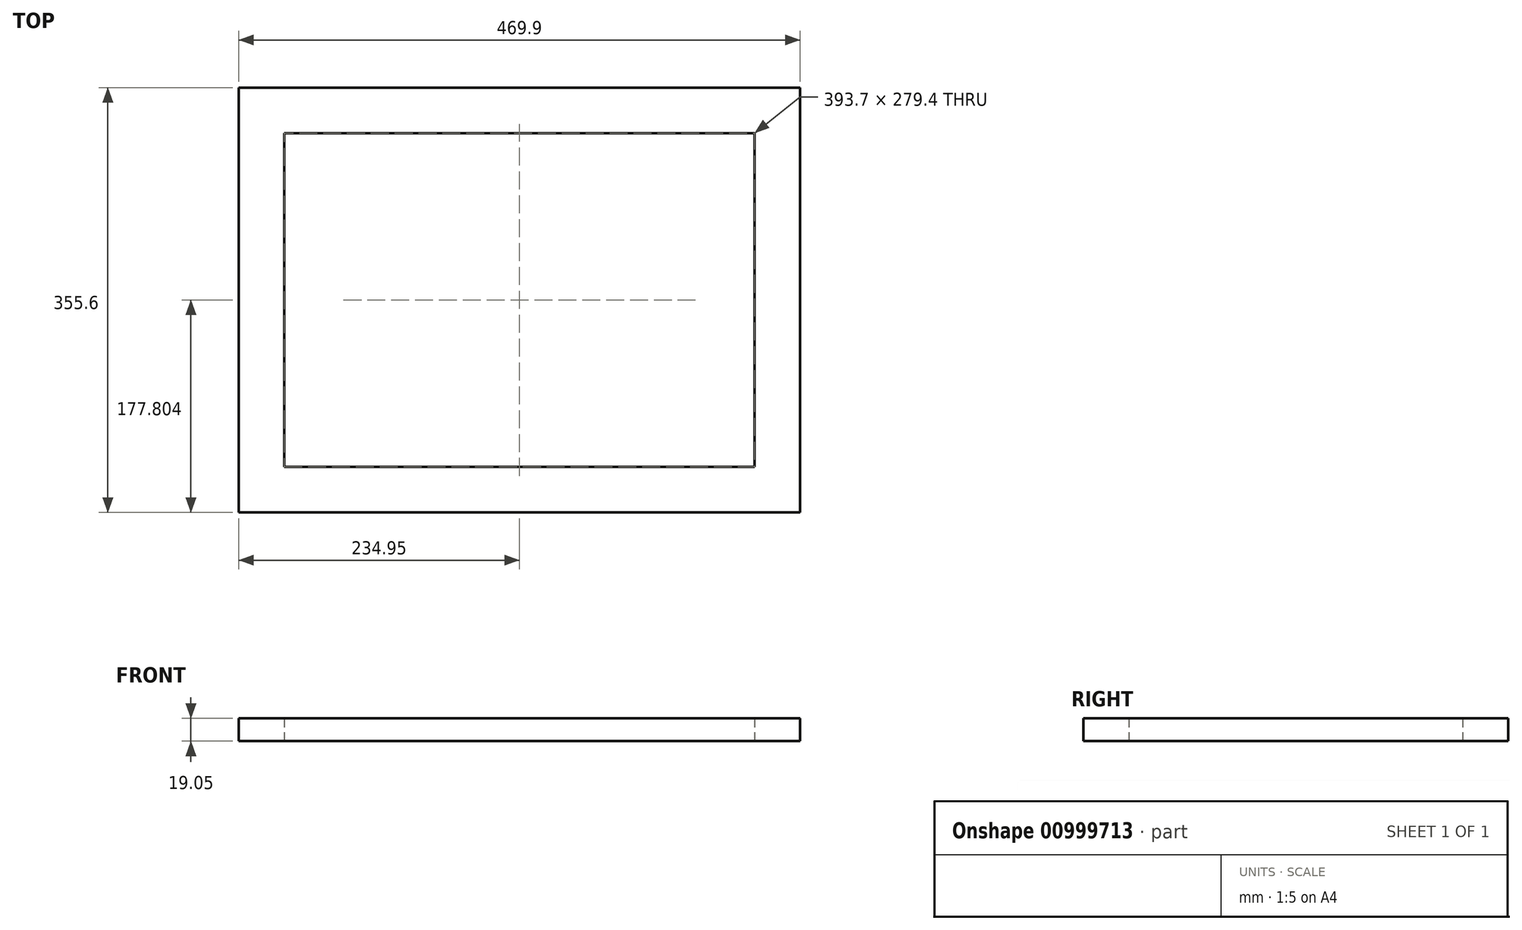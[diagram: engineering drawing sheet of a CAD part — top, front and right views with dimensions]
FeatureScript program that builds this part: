
annotation { "Feature Type Name" : "Feature", "Feature Type Description" : "" }
export const myFeature = defineFeature(function(context is Context, id is Id, definition is map)
    precondition{}
    {
        {
            var Q0;
            Q0=qCreatedBy(makeId("Top.planeOp"),FACE);
            var sketch = newSketch(context, id + "F0", { "sketchPlane" : qUnion([Q0])});
            skLineSegment(sketch, "E0.bottom", {"start": v(0, 20.24) * mm, "end": v(393.7, 20.24) * mm});
            skLineSegment(sketch, "E0.top", {"start": v(0, -17.86) * mm, "end": v(393.7, -17.86) * mm});
            skLineSegment(sketch, "E0.left", {"start": v(0, 20.24) * mm, "end": v(0, -17.86) * mm});
            skLineSegment(sketch, "E0.right", {"start": v(393.7, 20.24) * mm, "end": v(393.7, -17.86) * mm});
            skLineSegment(sketch, "E1.bottom", {"start": v(-38.1, 20.24) * mm, "end": v(0, 20.24) * mm});
            skLineSegment(sketch, "E1.top", {"start": v(-38.1, -335.36) * mm, "end": v(0, -335.36) * mm});
            skLineSegment(sketch, "E1.left", {"start": v(-38.1, 20.24) * mm, "end": v(-38.1, -335.36) * mm});
            skLineSegment(sketch, "E1.right", {"start": v(0, 20.24) * mm, "end": v(0, -335.36) * mm});
            skLineSegment(sketch, "E2.bottom", {"start": v(393.7, 20.24) * mm, "end": v(431.8, 20.24) * mm});
            skLineSegment(sketch, "E2.top", {"start": v(393.7, -335.36) * mm, "end": v(431.8, -335.36) * mm});
            skLineSegment(sketch, "E2.left", {"start": v(393.7, 20.24) * mm, "end": v(393.7, -335.36) * mm});
            skLineSegment(sketch, "E2.right", {"start": v(431.8, 20.24) * mm, "end": v(431.8, -335.36) * mm});
            skLineSegment(sketch, "E3.bottom", {"start": v(0, -335.36) * mm, "end": v(393.7, -335.36) * mm});
            skLineSegment(sketch, "E3.top", {"start": v(0, -297.26) * mm, "end": v(393.7, -297.26) * mm});
            skLineSegment(sketch, "E3.left", {"start": v(0, -335.36) * mm, "end": v(0, -297.26) * mm});
            skLineSegment(sketch, "E3.right", {"start": v(393.7, -335.36) * mm, "end": v(393.7, -297.26) * mm});
            skSolve(sketch);
        }
        {
            var Q0;
            {var subQ0=sQuery(id+"F0.wireOp",EDGE,"E0.bottom");Q0=makeQuery(id+"F0.imprint","IMPRINT",FACE,{"disambiguationData":[TD([[makeQuery(id+"F0.imprint","IMPRINT",EDGE,{"derivedFrom":subQ0}),-1.0]])]});}
            var Q1;
            {var subQ1=sQuery(id+"F0.wireOp",EDGE,"E1.bottom");Q1=makeQuery(id+"F0.imprint","IMPRINT",FACE,{"disambiguationData":[TD([[makeQuery(id+"F0.imprint","IMPRINT",EDGE,{"derivedFrom":subQ1}),-1.0]])]});}
            var Q2;
            Q2=makeQuery(id+"F0.imprint","IMPRINT",FACE,{"disambiguationData":[TD([[makeQuery(id+"F0.imprint","IMPRINT",EDGE,{"derivedFrom":sQuery(id+"F0.wireOp",EDGE,"E3.bottom")}),1.0]])]});
            var Q3;
            {var subQ3=sQuery(id+"F0.wireOp",EDGE,"E2.bottom");Q3=makeQuery(id+"F0.imprint","IMPRINT",FACE,{"disambiguationData":[TD([[makeQuery(id+"F0.imprint","IMPRINT",EDGE,{"derivedFrom":subQ3}),-1.0]])]});}
            extrude(context, id + "F1", {"entities" : qUnion([Q0, Q1, Q2, Q3]), "depth" : 19.05 * mm, "offsetDistance" : 25.4 * mm});
        }
    });
